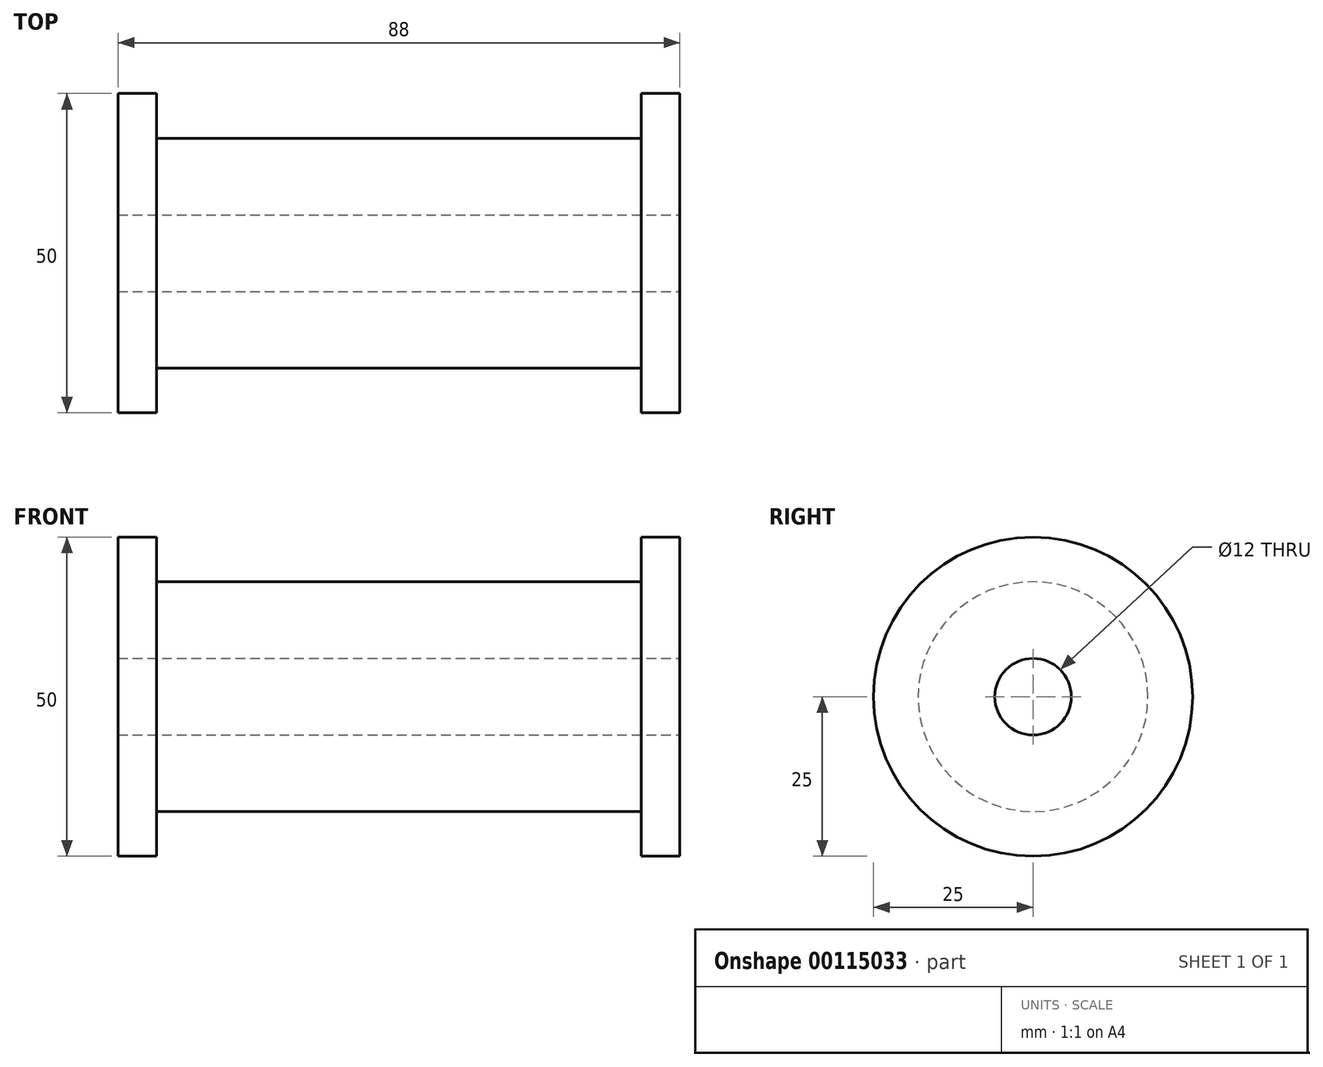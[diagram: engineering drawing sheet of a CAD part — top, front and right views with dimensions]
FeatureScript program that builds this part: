
annotation { "Feature Type Name" : "Feature", "Feature Type Description" : "" }
export const myFeature = defineFeature(function(context is Context, id is Id, definition is map)
    precondition{}
    {
        {
            var Q0;
            Q0=qCreatedBy(makeId("Front.planeOp"),FACE);
            var sketch = newSketch(context, id + "F0", { "sketchPlane" : qUnion([Q0])});
            skLineSegment(sketch, "E0.bottom", {"start": v(0, 0) * mm, "end": v(-38, 0) * mm});
            skLineSegment(sketch, "E0.top", {"start": v(0, 18) * mm, "end": v(-38, 18) * mm});
            skLineSegment(sketch, "E0.left", {"start": v(0, 0) * mm, "end": v(0, 18) * mm});
            skLineSegment(sketch, "E0.right", {"start": v(-38, 0) * mm, "end": v(-38, 18) * mm});
            skLineSegment(sketch, "E1.bottom", {"start": v(-38, 0) * mm, "end": v(-44, 0) * mm});
            skLineSegment(sketch, "E1.top", {"start": v(-38, 25) * mm, "end": v(-44, 25) * mm});
            skLineSegment(sketch, "E1.left", {"start": v(-38, 0) * mm, "end": v(-38, 25) * mm});
            skLineSegment(sketch, "E1.right", {"start": v(-44, 0) * mm, "end": v(-44, 25) * mm});
            skLineSegment(sketch, "E2.MirrorCS", {"start": v(0, 18) * mm, "end": v(38, 18) * mm});
            skLineSegment(sketch, "E3.MirrorCS", {"start": v(38, 0) * mm, "end": v(38, 25) * mm});
            skLineSegment(sketch, "E4.MirrorCS", {"start": v(38, 25) * mm, "end": v(44, 25) * mm});
            skLineSegment(sketch, "E5.MirrorCS", {"start": v(44, 0) * mm, "end": v(44, 25) * mm});
            skLineSegment(sketch, "E6.MirrorCS", {"start": v(38, 0) * mm, "end": v(44, 0) * mm});
            skLineSegment(sketch, "E7.MirrorCS", {"start": v(0, 0) * mm, "end": v(38, 0) * mm});
            skSolve(sketch);
        }
        {
            var Q0;
            {var subQ3=sQuery(id+"F0.wireOp",EDGE,"E1.bottom");Q0=makeQuery(id+"F0.imprint","IMPRINT",FACE,{"disambiguationData":[TD([[makeQuery(id+"F0.imprint","IMPRINT",EDGE,{"derivedFrom":subQ3}),-1.0]])]});}
            var Q1;
            {var subQ0=sQuery(id+"F0.wireOp",EDGE,"E0.bottom");Q1=makeQuery(id+"F0.imprint","IMPRINT",FACE,{"disambiguationData":[TD([[makeQuery(id+"F0.imprint","IMPRINT",EDGE,{"derivedFrom":subQ0}),-1.0]])]});}
            var Q2;
            Q2=makeQuery(id+"F0.imprint","IMPRINT",FACE,{"disambiguationData":[TD([[makeQuery(id+"F0.imprint","IMPRINT",EDGE,{"derivedFrom":sQuery(id+"F0.wireOp",EDGE,"E0.left")}),-1.0]])]});
            var Q3;
            {var subQ0=sQuery(id+"F0.wireOp",EDGE,"E4.MirrorCS");Q3=makeQuery(id+"F0.imprint","IMPRINT",FACE,{"disambiguationData":[TD([[makeQuery(id+"F0.imprint","IMPRINT",EDGE,{"derivedFrom":subQ0}),-1.0]])]});}
            var Q4;
            Q4=sQuery(id+"F0.wireOp",EDGE,"E0.bottom");
            revolve(context, id + "F1", {"entities" : qUnion([Q0, Q1, Q2, Q3]), "axis" : qUnion([Q4]), "revolveType" : RevolveType.FULL});
        }
        {
            var Q0;
            Q0=makeQuery(id+"F1.opRevolve","SWEPT_FACE",FACE,{"disambiguationData":[OSD([sQuery(id+"F0.wireOp",EDGE,"E5.MirrorCS")])]});
            var sketch = newSketch(context, id + "F2", { "sketchPlane" : qUnion([Q0])});
            skPoint(sketch, "E8", {"position": v(0, 0) * mm});
            skSolve(sketch);
        }
        {
            var Q0;
            Q0=sQuery(id+"F2.wireOp",VERTEX,"E8");
            var Q1;
            Q1=makeQuery(id+"F1.opRevolve","SWEPT_BODY",BODY,{"disambiguationData":[OSD([sQuery(id+"F0.wireOp",EDGE,"E0.bottom"),sQuery(id+"F0.wireOp",EDGE,"E0.top"),sQuery(id+"F0.wireOp",EDGE,"E1.bottom"),sQuery(id+"F0.wireOp",EDGE,"E1.top"),sQuery(id+"F0.wireOp",EDGE,"E1.left"),sQuery(id+"F0.wireOp",EDGE,"E1.right"),sQuery(id+"F0.wireOp",EDGE,"E2.MirrorCS"),sQuery(id+"F0.wireOp",EDGE,"E3.MirrorCS"),sQuery(id+"F0.wireOp",EDGE,"E4.MirrorCS"),sQuery(id+"F0.wireOp",EDGE,"E5.MirrorCS"),sQuery(id+"F0.wireOp",EDGE,"E6.MirrorCS"),sQuery(id+"F0.wireOp",EDGE,"E7.MirrorCS")])]});
            hole(context, id + "F3", {"style" : HoleStyle.SIMPLE, "endStyle" : HoleEndStyle.THROUGH, "holeDiameter" : 12 * mm, "locations" : qUnion([Q0]), "scope" : qUnion([Q1]), "isTappedThrough" : true});
        }
    });
